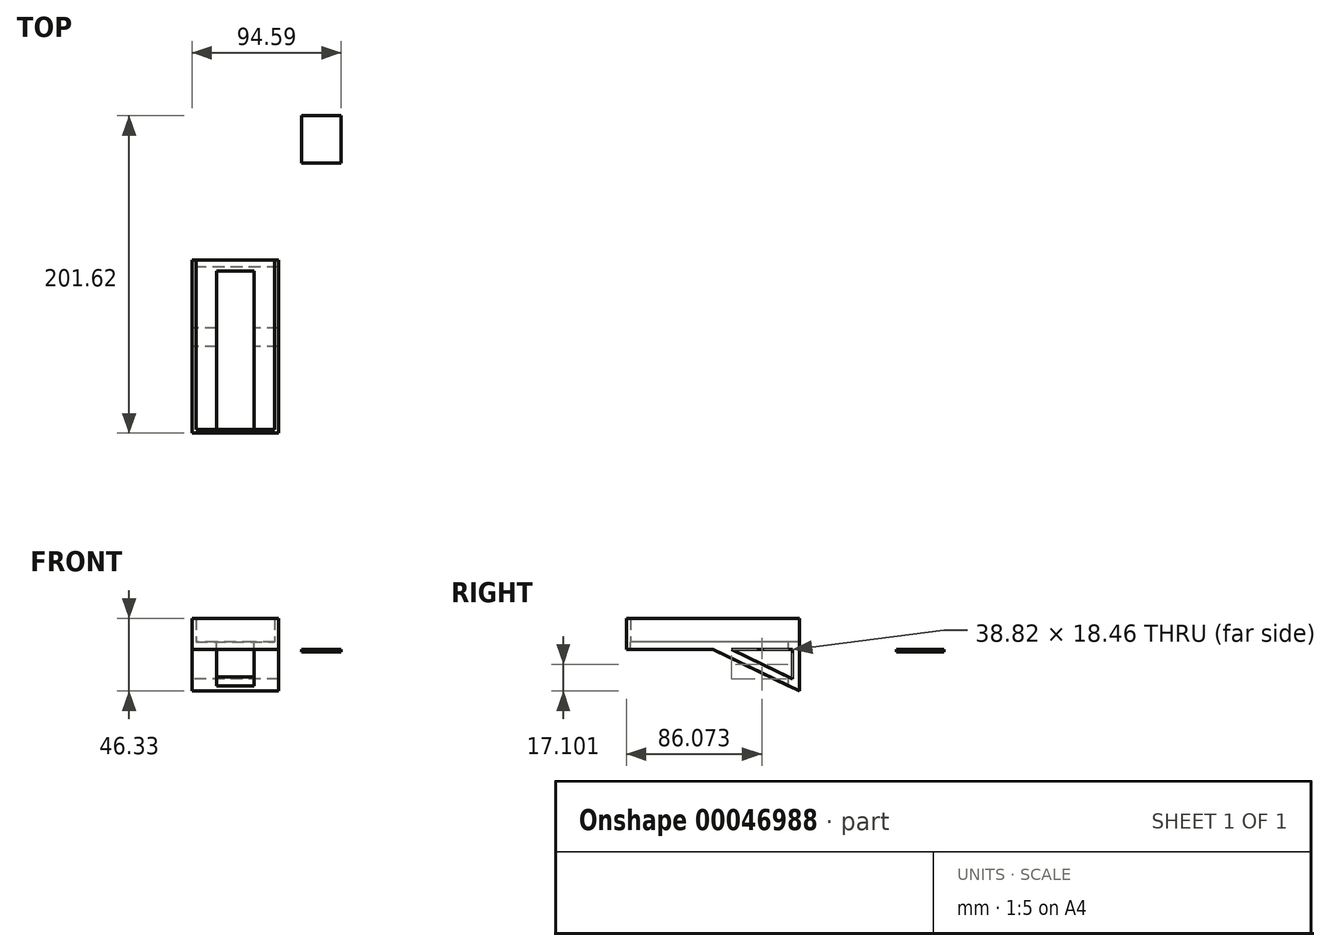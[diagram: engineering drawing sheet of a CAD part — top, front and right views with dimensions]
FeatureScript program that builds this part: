
annotation { "Feature Type Name" : "Feature", "Feature Type Description" : "" }
export const myFeature = defineFeature(function(context is Context, id is Id, definition is map)
    precondition{}
    {
        {
            var Q0;
            Q0=qCreatedBy(makeId("Front.planeOp"),FACE);
            var sketch = newSketch(context, id + "F0", { "sketchPlane" : qUnion([Q0])});
            skLineSegment(sketch, "E0.bottom", {"start": v(-69.6, 31.33) * mm, "end": v(-14.6, 31.33) * mm});
            skLineSegment(sketch, "E0.top", {"start": v(-69.6, 26.33) * mm, "end": v(-14.6, 26.33) * mm});
            skLineSegment(sketch, "E0.left", {"start": v(-69.6, 31.33) * mm, "end": v(-69.6, 26.33) * mm});
            skLineSegment(sketch, "E0.right", {"start": v(-14.6, 31.33) * mm, "end": v(-14.6, 26.33) * mm});
            skSolve(sketch);
        }
        {
            var Q0;
            Q0=makeQuery(id+"F0.imprint","IMPRINT",FACE,{"disambiguationData":[TD([[makeQuery(id+"F0.imprint","IMPRINT",EDGE,{"derivedFrom":sQuery(id+"F0.wireOp",EDGE,"E0.bottom")}),-1.0]])]});
            extrude(context, id + "F1", {"entities" : qUnion([Q0]), "depth" : 110 * mm});
        }
        {
            var Q0;
            Q0=makeQuery(id+"F1.opExtrude","SWEPT_FACE",FACE,{"disambiguationData":[OSD([sQuery(id+"F0.wireOp",EDGE,"E0.left")])]});
            var sketch = newSketch(context, id + "F2", { "sketchPlane" : qUnion([Q0])});
            skLineSegment(sketch, "E1.0", {"start": v(0, 31.33) * mm, "end": v(0, 26.33) * mm});
            skLineSegment(sketch, "E2.0", {"start": v(110, 26.33) * mm, "end": v(0, 26.33) * mm});
            skPoint(sketch, "E3", {"position": v(55, 26.33) * mm});
            skLineSegment(sketch, "E4", {"start": v(0, 26.33) * mm, "end": v(0, 0) * mm});
            skLineSegment(sketch, "E5", {"start": v(0, 0) * mm, "end": v(55, 26.33) * mm});
            skSolve(sketch);
        }
        {
            var Q0;
            {var subQ0=sQuery(id+"F2.wireOp",EDGE,"E4");Q0=makeQuery(id+"F2.imprint","IMPRINT",FACE,{"disambiguationData":[TD([[makeQuery(id+"F2.imprint","IMPRINT",EDGE,{"derivedFrom":subQ0}),1.0]])]});}
            var Q1;
            Q1=makeQuery(id+"F1.opExtrude","SWEPT_FACE",FACE,{"disambiguationData":[OSD([sQuery(id+"F0.wireOp",EDGE,"E0.right")])]});
            extrude(context, id + "F3", {"entities" : qUnion([Q0]), "operationType" : NewBodyOperationType.ADD, "endBound" : BoundingType.UP_TO_SURFACE, "oppositeDirection" : true, "endBoundEntityFace" : qUnion([Q1]), "depth" : 25 * mm});
        }
        {
            var Q0;
            Q0=makeQuery(id+"F1.opExtrude","SWEPT_FACE",FACE,{"disambiguationData":[OSD([sQuery(id+"F0.wireOp",EDGE,"E0.bottom")])]});
            var sketch = newSketch(context, id + "F4", { "sketchPlane" : qUnion([Q0])});
            skPoint(sketch, "E6", {"position": v(-30.21, 0) * mm});
            skPoint(sketch, "E7", {"position": v(-53.97, 0) * mm});
            skLineSegment(sketch, "E8", {"start": v(-53.97, 0) * mm, "end": v(-69.6, 0) * mm});
            skLineSegment(sketch, "E9", {"start": v(-30.21, 0) * mm, "end": v(-14.6, 0) * mm});
            skPoint(sketch, "E10", {"position": v(-67.1, 0) * mm});
            skPoint(sketch, "E11", {"position": v(-17.1, 0) * mm});
            skLineSegment(sketch, "E12.0", {"start": v(-69.6, -110) * mm, "end": v(-14.6, -110) * mm});
            skLineSegment(sketch, "E13", {"start": v(-67.1, 0) * mm, "end": v(-67.1, -107.5) * mm});
            skLineSegment(sketch, "E14", {"start": v(-17.1, 0) * mm, "end": v(-17.1, -107.5) * mm});
            skLineSegment(sketch, "E15", {"start": v(-17.1, -107.5) * mm, "end": v(-67.1, -107.5) * mm});
            skLineSegment(sketch, "E16", {"start": v(-53.97, 0) * mm, "end": v(-53.97, -107.5) * mm});
            skLineSegment(sketch, "E17", {"start": v(-30.21, 0) * mm, "end": v(-30.21, -107.5) * mm});
            skPoint(sketch, "E18", {"position": v(-30.21, -6.92) * mm});
            skLineSegment(sketch, "E19", {"start": v(-30.21, -6.92) * mm, "end": v(-53.97, -6.92) * mm});
            skSolve(sketch);
        }
        {
            var Q0;
            Q0=makeQuery(id+"F4.imprint","IMPRINT",FACE,{"disambiguationData":[TD([[makeQuery(id+"F4.imprint","IMPRINT",EDGE,{"derivedFrom":sQuery(id+"F4.wireOp",EDGE,"E12.0")}),1.0]])]});
            extrude(context, id + "F5", {"entities" : qUnion([Q0]), "operationType" : NewBodyOperationType.ADD, "depth" : 15 * mm});
        }
        {
            var Q0;
            {var subQ5=sQuery(id+"F4.wireOp",EDGE,"E19");Q0=makeQuery(id+"F4.imprint","IMPRINT",FACE,{"disambiguationData":[TD([[makeQuery(id+"F4.imprint","IMPRINT",EDGE,{"derivedFrom":subQ5}),1.0]])]});}
            extrude(context, id + "F6", {"entities" : qUnion([Q0]), "operationType" : NewBodyOperationType.REMOVE, "endBound" : BoundingType.THROUGH_ALL, "oppositeDirection" : true, "depth" : 25 * mm});
        }
        {
            var Q0;
            {var subQ0=sQuery(id+"F0.wireOp",EDGE,"E0.left");Q0=makeQuery(id+"F5.boolean.opBoolean","MERGE",FACE,{"derivedFrom":[makeQuery(id+"F3.boolean.opBoolean","MERGE",FACE,{"derivedFrom":[makeQuery(id+"F1.opExtrude","SWEPT_FACE",FACE,{"disambiguationData":[OSD([subQ0])]}),makeQuery(id+"F3.opExtrude","CAP_FACE",FACE,{"disambiguationData":[OSD([sQuery(id+"F2.wireOp",EDGE,"E2.0"),sQuery(id+"F2.wireOp",EDGE,"E4"),sQuery(id+"F2.wireOp",EDGE,"E5")])],"isStart":true})]}),makeQuery(id+"F5.opExtrude","SWEPT_FACE",FACE,{"disambiguationData":[OSD([sQuery(id+"F0.wireOp",EDGE,"E0.bottom"),subQ0])]})]});}
            var sketch = newSketch(context, id + "F7", { "sketchPlane" : qUnion([Q0])});
            skPoint(sketch, "E20.0", {"position": v(0, 31.33) * mm});
            skLineSegment(sketch, "E21.0", {"start": v(0, 0) * mm, "end": v(55, 26.33) * mm});
            skLineSegment(sketch, "E22", {"start": v(0, 0) * mm, "end": v(0, 26.33) * mm});
            skLineSegment(sketch, "E23", {"start": v(0, 26.33) * mm, "end": v(55, 26.33) * mm});
            skLineSegment(sketch, "E24.1", {"start": v(4.52, 7.87) * mm, "end": v(4.52, 21.3) * mm});
            skLineSegment(sketch, "E24.2", {"start": v(4.52, 7.87) * mm, "end": v(32.81, 21.3) * mm});
            skLineSegment(sketch, "E25", {"start": v(32.81, 21.3) * mm, "end": v(43.34, 26.33) * mm});
            skLineSegment(sketch, "E26", {"start": v(4.52, 21.3) * mm, "end": v(4.52, 26.33) * mm});
            skSolve(sketch);
        }
        {
            var Q0;
            Q0=makeQuery(id+"F7.imprint","IMPRINT",FACE,{"disambiguationData":[TD([[makeQuery(id+"F7.imprint","IMPRINT",EDGE,{"derivedFrom":sQuery(id+"F7.wireOp",EDGE,"E24.1")}),-1.0]])]});
            extrude(context, id + "F8", {"entities" : qUnion([Q0]), "operationType" : NewBodyOperationType.REMOVE, "endBound" : BoundingType.THROUGH_ALL, "oppositeDirection" : true, "depth" : 25 * mm});
        }
        {
            var Q0;
            Q0=qCreatedBy(makeId("Right.planeOp"),FACE);
            var sketch = newSketch(context, id + "F9", { "sketchPlane" : qUnion([Q0])});
            skLineSegment(sketch, "E27.bottom", {"start": v(91.62, 25) * mm, "end": v(61.62, 25) * mm});
            skLineSegment(sketch, "E27.top", {"start": v(91.62, 26.5) * mm, "end": v(61.62, 26.5) * mm});
            skLineSegment(sketch, "E27.left", {"start": v(91.62, 25) * mm, "end": v(91.62, 26.5) * mm});
            skLineSegment(sketch, "E27.right", {"start": v(61.62, 25) * mm, "end": v(61.62, 26.5) * mm});
            skSolve(sketch);
        }
        {
            var Q0;
            Q0=makeQuery(id+"F9.imprint","IMPRINT",FACE,{"disambiguationData":[TD([[makeQuery(id+"F9.imprint","IMPRINT",EDGE,{"derivedFrom":sQuery(id+"F9.wireOp",EDGE,"E27.bottom")}),-1.0]])]});
            extrude(context, id + "F10", {"entities" : qUnion([Q0]), "depth" : 25 * mm});
        }
    });
